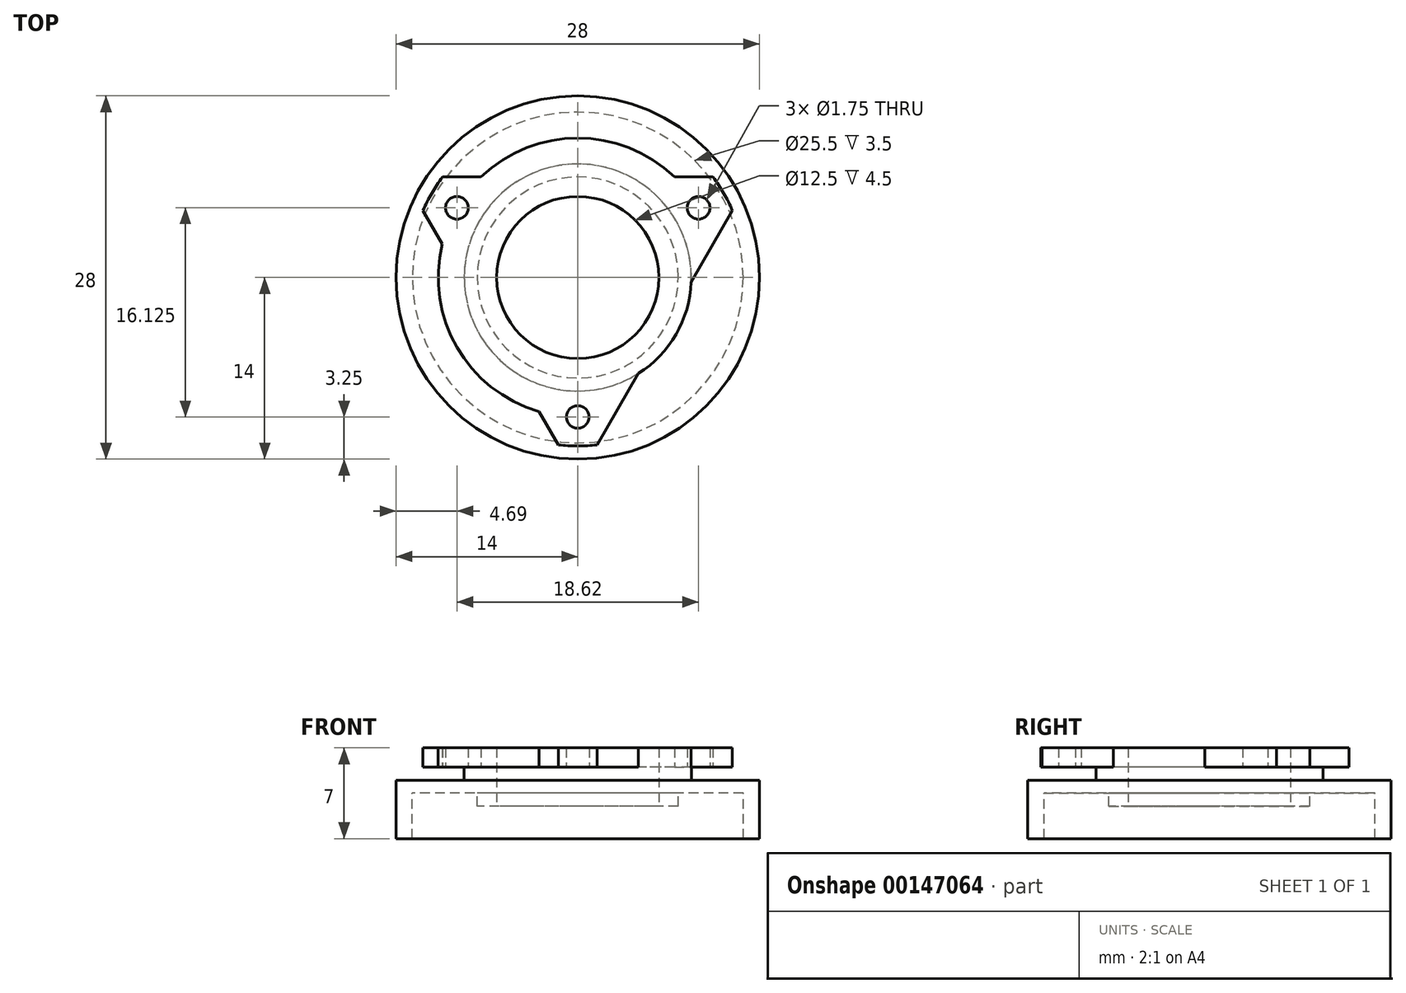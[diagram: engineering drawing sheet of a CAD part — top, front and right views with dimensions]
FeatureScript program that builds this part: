
annotation { "Feature Type Name" : "Feature", "Feature Type Description" : "" }
export const myFeature = defineFeature(function(context is Context, id is Id, definition is map)
    precondition{}
    {
        {
            var Q0;
            Q0=qCreatedBy(makeId("Top.planeOp"),FACE);
            var sketch = newSketch(context, id + "F0", { "sketchPlane" : qUnion([Q0])});
            skCircle(sketch, "E0", {"center": v(0, 0) * mm, "radius": 14 * mm});
            skCircle(sketch, "E1", {"center": v(0, 0) * mm, "radius": 12.75 * mm});
            skCircle(sketch, "E2", {"center": v(0, 0) * mm, "radius": 8.75 * mm});
            skCircle(sketch, "E3", {"center": v(0, 0) * mm, "radius": 7.75 * mm});
            skSolve(sketch);
        }
        {
            var Q0;
            Q0=makeQuery(id+"F0.imprint","IMPRINT",FACE,{"disambiguationData":[TD([[makeQuery(id+"F0.imprint","IMPRINT",EDGE,{"derivedFrom":sQuery(id+"F0.wireOp",EDGE,"E2")}),1.0]])]});
            extrude(context, id + "F1", {"entities" : qUnion([Q0]), "depth" : 2 * mm});
        }
        {
            var Q0;
            Q0=makeQuery(id+"F0.imprint","IMPRINT",FACE,{"disambiguationData":[TD([[makeQuery(id+"F0.imprint","IMPRINT",EDGE,{"derivedFrom":sQuery(id+"F0.wireOp",EDGE,"E1")}),1.0]])]});
            extrude(context, id + "F2", {"entities" : qUnion([Q0]), "operationType" : NewBodyOperationType.ADD, "depth" : 1 * mm});
        }
        {
            var Q0;
            Q0=makeQuery(id+"F0.imprint","IMPRINT",FACE,{"disambiguationData":[TD([[makeQuery(id+"F0.imprint","IMPRINT",EDGE,{"derivedFrom":sQuery(id+"F0.wireOp",EDGE,"E0")}),1.0]])]});
            extrude(context, id + "F3", {"entities" : qUnion([Q0]), "operationType" : NewBodyOperationType.ADD, "oppositeDirection" : true, "depth" : 3.5 * mm, "hasSecondDirection" : true, "secondDirectionOppositeDirection" : false, "secondDirectionDepth" : 1 * mm});
        }
        {
            var Q0;
            Q0=makeQuery(id+"F1.opExtrude","CAP_FACE",FACE,{"disambiguationData":[OSD([sQuery(id+"F0.wireOp",EDGE,"E2"),sQuery(id+"F0.wireOp",EDGE,"E3")])],"isStart":false});
            var sketch = newSketch(context, id + "F4", { "sketchPlane" : qUnion([Q0])});
            skCircle(sketch, "E4", {"center": v(0, 0) * mm, "radius": 10.75 * mm});
            skLineSegment(sketch, "E5", {"start": v(-9.3, 5.38) * mm, "end": v(9.3, 5.38) * mm});
            skLineSegment(sketch, "E6", {"start": v(9.3, 5.38) * mm, "end": v(0, -10.75) * mm});
            skLineSegment(sketch, "E7", {"start": v(0, -10.75) * mm, "end": v(-9.3, 5.38) * mm});
            skCircle(sketch, "E8", {"center": v(-9.3, 5.38) * mm, "radius": 0.88 * mm});
            skCircle(sketch, "E9", {"center": v(0, -10.75) * mm, "radius": 0.88 * mm});
            skCircle(sketch, "E10", {"center": v(9.3, 5.38) * mm, "radius": 0.88 * mm});
            skCircle(sketch, "E11", {"center": v(0, 0) * mm, "radius": 12.99 * mm});
            skCircle(sketch, "E12.0", {"center": v(0, 0) * mm, "radius": 7.75 * mm});
            skCircle(sketch, "E13.0", {"center": v(0, 0) * mm, "radius": 6.25 * mm});
            skLineSegment(sketch, "E14.0", {"start": v(-13.42, 7.75) * mm, "end": v(13.42, 7.75) * mm});
            skLineSegment(sketch, "E14.1", {"start": v(0, -15.5) * mm, "end": v(-13.42, 7.75) * mm});
            skLineSegment(sketch, "E14.2", {"start": v(13.42, 7.75) * mm, "end": v(0, -15.5) * mm});
            skSolve(sketch);
        }
        {
            var Q0;
            {var subQ0=sQuery(id+"F4.wireOp",EDGE,"E14.0");var subQ6=sQuery(id+"F4.wireOp",EDGE,"E4");var subQ10=makeQuery(id+"F4.imprint","INTERSECT",VERTEX,{"disambiguationData":[OD(1.0)],"derivedFrom":[subQ6,subQ0]});Q0=makeQuery(id+"F4.imprint","IMPRINT",FACE,{"disambiguationData":[TD([[makeQuery(id+"F4.imprint","IMPRINT",EDGE,{"disambiguationData":[TD([[subQ10,-1.0]])],"derivedFrom":subQ6}),-1.0]])]});}
            var Q1;
            {var subQ0=sQuery(id+"F4.wireOp",EDGE,"E14.1");var subQ6=sQuery(id+"F4.wireOp",EDGE,"E4");var subQ10=makeQuery(id+"F4.imprint","INTERSECT",VERTEX,{"disambiguationData":[OD(1.0)],"derivedFrom":[subQ6,subQ0]});Q1=makeQuery(id+"F4.imprint","IMPRINT",FACE,{"disambiguationData":[TD([[makeQuery(id+"F4.imprint","IMPRINT",EDGE,{"disambiguationData":[TD([[subQ10,-1.0]])],"derivedFrom":subQ6}),-1.0]])]});}
            var Q2;
            {var subQ0=sQuery(id+"F4.wireOp",EDGE,"E10");var subQ1=sQuery(id+"F4.wireOp",EDGE,"E4");var subQ2=makeQuery(id+"F4.imprint","INTERSECT",VERTEX,{"disambiguationData":[OD(0.0)],"derivedFrom":[subQ1,subQ0]});Q2=makeQuery(id+"F4.imprint","IMPRINT",FACE,{"disambiguationData":[TD([[makeQuery(id+"F4.imprint","IMPRINT",EDGE,{"disambiguationData":[TD([[subQ2,1.0]])],"derivedFrom":subQ1}),-1.0]])]});}
            var Q3;
            {var subQ0=sQuery(id+"F4.wireOp",EDGE,"E14.0");var subQ1=sQuery(id+"F4.wireOp",EDGE,"E4");var subQ2=makeQuery(id+"F4.imprint","INTERSECT",VERTEX,{"disambiguationData":[OD(0.0)],"derivedFrom":[subQ1,subQ0]});Q3=makeQuery(id+"F4.imprint","IMPRINT",FACE,{"disambiguationData":[TD([[makeQuery(id+"F4.imprint","IMPRINT",EDGE,{"disambiguationData":[TD([[subQ2,-1.0]])],"derivedFrom":subQ1}),1.0]])]});}
            var Q4;
            {var subQ0=sQuery(id+"F4.wireOp",EDGE,"E14.0");var subQ1=sQuery(id+"F4.wireOp",EDGE,"E4");var subQ2=makeQuery(id+"F4.imprint","INTERSECT",VERTEX,{"disambiguationData":[OD(1.0)],"derivedFrom":[subQ1,subQ0]});Q4=makeQuery(id+"F4.imprint","IMPRINT",FACE,{"disambiguationData":[TD([[makeQuery(id+"F4.imprint","IMPRINT",EDGE,{"disambiguationData":[TD([[subQ2,-1.0]])],"derivedFrom":subQ1}),1.0]])]});}
            var Q5;
            {var subQ0=sQuery(id+"F4.wireOp",EDGE,"E8");var subQ1=sQuery(id+"F4.wireOp",EDGE,"E5");var subQ2=makeQuery(id+"F4.imprint","INTERSECT",VERTEX,{"derivedFrom":[subQ1,subQ0]});Q5=makeQuery(id+"F4.imprint","IMPRINT",FACE,{"disambiguationData":[TD([[makeQuery(id+"F4.imprint","IMPRINT",EDGE,{"disambiguationData":[TD([[subQ2,-1.0]])],"derivedFrom":subQ1}),-1.0]])]});}
            var Q6;
            {var subQ1=sQuery(id+"F4.wireOp",EDGE,"E4");var subQ5=sQuery(id+"F4.wireOp",EDGE,"E8");var subQ6=makeQuery(id+"F4.imprint","INTERSECT",VERTEX,{"disambiguationData":[OD(1.0)],"derivedFrom":[subQ1,subQ5]});Q6=makeQuery(id+"F4.imprint","IMPRINT",FACE,{"disambiguationData":[TD([[makeQuery(id+"F4.imprint","IMPRINT",EDGE,{"disambiguationData":[TD([[subQ6,-1.0]])],"derivedFrom":subQ1}),1.0]])]});}
            var Q7;
            {var subQ0=sQuery(id+"F4.wireOp",EDGE,"E14.1");var subQ1=sQuery(id+"F4.wireOp",EDGE,"E4");var subQ2=makeQuery(id+"F4.imprint","INTERSECT",VERTEX,{"disambiguationData":[OD(0.0)],"derivedFrom":[subQ1,subQ0]});Q7=makeQuery(id+"F4.imprint","IMPRINT",FACE,{"disambiguationData":[TD([[makeQuery(id+"F4.imprint","IMPRINT",EDGE,{"disambiguationData":[TD([[subQ2,-1.0]])],"derivedFrom":subQ1}),1.0]])]});}
            var Q8;
            {var subQ0=sQuery(id+"F4.wireOp",EDGE,"E14.1");var subQ1=sQuery(id+"F4.wireOp",EDGE,"E4");var subQ2=makeQuery(id+"F4.imprint","INTERSECT",VERTEX,{"disambiguationData":[OD(1.0)],"derivedFrom":[subQ1,subQ0]});Q8=makeQuery(id+"F4.imprint","IMPRINT",FACE,{"disambiguationData":[TD([[makeQuery(id+"F4.imprint","IMPRINT",EDGE,{"disambiguationData":[TD([[subQ2,-1.0]])],"derivedFrom":subQ1}),1.0]])]});}
            var Q9;
            {var subQ1=sQuery(id+"F4.wireOp",EDGE,"E4");var subQ5=sQuery(id+"F4.wireOp",EDGE,"E9");var subQ9=makeQuery(id+"F4.imprint","INTERSECT",VERTEX,{"disambiguationData":[OD(1.0)],"derivedFrom":[subQ1,subQ5]});Q9=makeQuery(id+"F4.imprint","IMPRINT",FACE,{"disambiguationData":[TD([[makeQuery(id+"F4.imprint","IMPRINT",EDGE,{"disambiguationData":[TD([[subQ9,-1.0]])],"derivedFrom":subQ1}),1.0]])]});}
            var Q10;
            {var subQ0=sQuery(id+"F4.wireOp",EDGE,"E14.2");var subQ1=sQuery(id+"F4.wireOp",EDGE,"E4");var subQ2=makeQuery(id+"F4.imprint","INTERSECT",VERTEX,{"disambiguationData":[OD(0.0)],"derivedFrom":[subQ1,subQ0]});Q10=makeQuery(id+"F4.imprint","IMPRINT",FACE,{"disambiguationData":[TD([[makeQuery(id+"F4.imprint","IMPRINT",EDGE,{"disambiguationData":[TD([[subQ2,1.0]])],"derivedFrom":subQ1}),1.0]])]});}
            var Q11;
            {var subQ1=sQuery(id+"F4.wireOp",EDGE,"E4");var subQ5=sQuery(id+"F4.wireOp",EDGE,"E10");var subQ6=makeQuery(id+"F4.imprint","INTERSECT",VERTEX,{"disambiguationData":[OD(0.0)],"derivedFrom":[subQ1,subQ5]});Q11=makeQuery(id+"F4.imprint","IMPRINT",FACE,{"disambiguationData":[TD([[makeQuery(id+"F4.imprint","IMPRINT",EDGE,{"disambiguationData":[TD([[subQ6,1.0]])],"derivedFrom":subQ1}),1.0]])]});}
            var Q12;
            {var subQ0=sQuery(id+"F4.wireOp",EDGE,"E10");var subQ1=sQuery(id+"F4.wireOp",EDGE,"E5");var subQ2=makeQuery(id+"F4.imprint","INTERSECT",VERTEX,{"derivedFrom":[subQ1,subQ0]});Q12=makeQuery(id+"F4.imprint","IMPRINT",FACE,{"disambiguationData":[TD([[makeQuery(id+"F4.imprint","IMPRINT",EDGE,{"disambiguationData":[TD([[subQ2,1.0]])],"derivedFrom":subQ1}),-1.0]])]});}
            var Q13;
            {var subQ1=sQuery(id+"F4.wireOp",EDGE,"E4");var subQ5=sQuery(id+"F4.wireOp",EDGE,"E10");var subQ6=makeQuery(id+"F4.imprint","INTERSECT",VERTEX,{"disambiguationData":[OD(1.0)],"derivedFrom":[subQ1,subQ5]});Q13=makeQuery(id+"F4.imprint","IMPRINT",FACE,{"disambiguationData":[TD([[makeQuery(id+"F4.imprint","IMPRINT",EDGE,{"disambiguationData":[TD([[subQ6,-1.0]])],"derivedFrom":subQ1}),1.0]])]});}
            var Q14;
            {var subQ0=sQuery(id+"F4.wireOp",EDGE,"E9");var subQ1=sQuery(id+"F4.wireOp",EDGE,"E6");var subQ2=makeQuery(id+"F4.imprint","INTERSECT",VERTEX,{"derivedFrom":[subQ1,subQ0]});Q14=makeQuery(id+"F4.imprint","IMPRINT",FACE,{"disambiguationData":[TD([[makeQuery(id+"F4.imprint","IMPRINT",EDGE,{"disambiguationData":[TD([[subQ2,1.0]])],"derivedFrom":subQ1}),-1.0]])]});}
            var Q15;
            {var subQ0=sQuery(id+"F4.wireOp",EDGE,"E14.0");var subQ1=makeQuery(id+"F4.imprint","INTERSECT",VERTEX,{"derivedFrom":[sQuery(id+"F4.wireOp",EDGE,"E12.0"),subQ0]});Q15=makeQuery(id+"F4.imprint","IMPRINT",FACE,{"disambiguationData":[TD([[makeQuery(id+"F4.imprint","IMPRINT",EDGE,{"disambiguationData":[TD([[subQ1,1.0]])],"derivedFrom":subQ0}),1.0]])]});}
            var Q16;
            {var subQ0=sQuery(id+"F4.wireOp",EDGE,"E12.0");var subQ1=sQuery(id+"F4.wireOp",EDGE,"E5");var subQ2=makeQuery(id+"F4.imprint","INTERSECT",VERTEX,{"disambiguationData":[OD(0.0)],"derivedFrom":[subQ1,subQ0]});Q16=makeQuery(id+"F4.imprint","IMPRINT",FACE,{"disambiguationData":[TD([[makeQuery(id+"F4.imprint","IMPRINT",EDGE,{"disambiguationData":[TD([[subQ2,1.0]])],"derivedFrom":subQ1}),1.0]])]});}
            var Q17;
            {var subQ0=sQuery(id+"F4.wireOp",EDGE,"E12.0");var subQ1=sQuery(id+"F4.wireOp",EDGE,"E5");var subQ2=makeQuery(id+"F4.imprint","INTERSECT",VERTEX,{"disambiguationData":[OD(0.0)],"derivedFrom":[subQ1,subQ0]});Q17=makeQuery(id+"F4.imprint","IMPRINT",FACE,{"disambiguationData":[TD([[makeQuery(id+"F4.imprint","IMPRINT",EDGE,{"disambiguationData":[TD([[subQ2,1.0]])],"derivedFrom":subQ1}),-1.0]])]});}
            var Q18;
            {var subQ0=sQuery(id+"F4.wireOp",EDGE,"E12.0");var subQ1=sQuery(id+"F4.wireOp",EDGE,"E7");var subQ2=makeQuery(id+"F4.imprint","INTERSECT",VERTEX,{"disambiguationData":[OD(1.0)],"derivedFrom":[subQ1,subQ0]});Q18=makeQuery(id+"F4.imprint","IMPRINT",FACE,{"disambiguationData":[TD([[makeQuery(id+"F4.imprint","IMPRINT",EDGE,{"disambiguationData":[TD([[subQ2,-1.0]])],"derivedFrom":subQ1}),1.0]])]});}
            var Q19;
            {var subQ0=sQuery(id+"F4.wireOp",EDGE,"E14.1");var subQ1=makeQuery(id+"F4.imprint","INTERSECT",VERTEX,{"derivedFrom":[sQuery(id+"F4.wireOp",EDGE,"E12.0"),subQ0]});Q19=makeQuery(id+"F4.imprint","IMPRINT",FACE,{"disambiguationData":[TD([[makeQuery(id+"F4.imprint","IMPRINT",EDGE,{"disambiguationData":[TD([[subQ1,1.0]])],"derivedFrom":subQ0}),1.0]])]});}
            var Q20;
            {var subQ0=sQuery(id+"F4.wireOp",EDGE,"E12.0");var subQ1=sQuery(id+"F4.wireOp",EDGE,"E7");var subQ2=makeQuery(id+"F4.imprint","INTERSECT",VERTEX,{"disambiguationData":[OD(0.0)],"derivedFrom":[subQ1,subQ0]});Q20=makeQuery(id+"F4.imprint","IMPRINT",FACE,{"disambiguationData":[TD([[makeQuery(id+"F4.imprint","IMPRINT",EDGE,{"disambiguationData":[TD([[subQ2,1.0]])],"derivedFrom":subQ1}),1.0]])]});}
            var Q21;
            {var subQ0=sQuery(id+"F4.wireOp",EDGE,"E12.0");var subQ1=sQuery(id+"F4.wireOp",EDGE,"E6");var subQ2=makeQuery(id+"F4.imprint","INTERSECT",VERTEX,{"disambiguationData":[OD(1.0)],"derivedFrom":[subQ1,subQ0]});Q21=makeQuery(id+"F4.imprint","IMPRINT",FACE,{"disambiguationData":[TD([[makeQuery(id+"F4.imprint","IMPRINT",EDGE,{"disambiguationData":[TD([[subQ2,-1.0]])],"derivedFrom":subQ1}),-1.0]])]});}
            var Q22;
            {var subQ0=sQuery(id+"F4.wireOp",EDGE,"E12.0");var subQ1=sQuery(id+"F4.wireOp",EDGE,"E6");var subQ2=makeQuery(id+"F4.imprint","INTERSECT",VERTEX,{"disambiguationData":[OD(1.0)],"derivedFrom":[subQ1,subQ0]});Q22=makeQuery(id+"F4.imprint","IMPRINT",FACE,{"disambiguationData":[TD([[makeQuery(id+"F4.imprint","IMPRINT",EDGE,{"disambiguationData":[TD([[subQ2,-1.0]])],"derivedFrom":subQ1}),1.0]])]});}
            var Q23;
            {var subQ0=sQuery(id+"F4.wireOp",EDGE,"E14.2");var subQ1=makeQuery(id+"F4.imprint","INTERSECT",VERTEX,{"derivedFrom":[sQuery(id+"F4.wireOp",EDGE,"E12.0"),subQ0]});Q23=makeQuery(id+"F4.imprint","IMPRINT",FACE,{"disambiguationData":[TD([[makeQuery(id+"F4.imprint","IMPRINT",EDGE,{"disambiguationData":[TD([[subQ1,1.0]])],"derivedFrom":subQ0}),1.0]])]});}
            var Q24;
            {var subQ0=sQuery(id+"F4.wireOp",EDGE,"E12.0");var subQ1=sQuery(id+"F4.wireOp",EDGE,"E6");var subQ2=makeQuery(id+"F4.imprint","INTERSECT",VERTEX,{"disambiguationData":[OD(0.0)],"derivedFrom":[subQ1,subQ0]});Q24=makeQuery(id+"F4.imprint","IMPRINT",FACE,{"disambiguationData":[TD([[makeQuery(id+"F4.imprint","IMPRINT",EDGE,{"disambiguationData":[TD([[subQ2,1.0]])],"derivedFrom":subQ1}),1.0]])]});}
            var Q25;
            {var subQ0=sQuery(id+"F4.wireOp",EDGE,"E12.0");var subQ1=sQuery(id+"F4.wireOp",EDGE,"E5");var subQ2=makeQuery(id+"F4.imprint","INTERSECT",VERTEX,{"disambiguationData":[OD(1.0)],"derivedFrom":[subQ1,subQ0]});Q25=makeQuery(id+"F4.imprint","IMPRINT",FACE,{"disambiguationData":[TD([[makeQuery(id+"F4.imprint","IMPRINT",EDGE,{"disambiguationData":[TD([[subQ2,-1.0]])],"derivedFrom":subQ1}),-1.0]])]});}
            var Q26;
            {var subQ0=sQuery(id+"F4.wireOp",EDGE,"E12.0");var subQ1=sQuery(id+"F4.wireOp",EDGE,"E5");var subQ2=makeQuery(id+"F4.imprint","INTERSECT",VERTEX,{"disambiguationData":[OD(1.0)],"derivedFrom":[subQ1,subQ0]});Q26=makeQuery(id+"F4.imprint","IMPRINT",FACE,{"disambiguationData":[TD([[makeQuery(id+"F4.imprint","IMPRINT",EDGE,{"disambiguationData":[TD([[subQ2,-1.0]])],"derivedFrom":subQ1}),1.0]])]});}
            var Q27;
            {var subQ0=sQuery(id+"F4.wireOp",EDGE,"E12.0");var subQ1=sQuery(id+"F4.wireOp",EDGE,"E5");var subQ4=makeQuery(id+"F4.imprint","INTERSECT",VERTEX,{"disambiguationData":[OD(0.0)],"derivedFrom":[subQ1,subQ0]});Q27=makeQuery(id+"F4.imprint","IMPRINT",FACE,{"disambiguationData":[TD([[makeQuery(id+"F4.imprint","IMPRINT",EDGE,{"disambiguationData":[TD([[subQ4,-1.0]])],"derivedFrom":subQ1}),1.0]])]});}
            var Q28;
            {var subQ0=sQuery(id+"F4.wireOp",EDGE,"E12.0");var subQ1=sQuery(id+"F4.wireOp",EDGE,"E5");var subQ2=makeQuery(id+"F4.imprint","INTERSECT",VERTEX,{"disambiguationData":[OD(0.0)],"derivedFrom":[subQ1,subQ0]});Q28=makeQuery(id+"F4.imprint","IMPRINT",FACE,{"disambiguationData":[TD([[makeQuery(id+"F4.imprint","IMPRINT",EDGE,{"disambiguationData":[TD([[subQ2,-1.0]])],"derivedFrom":subQ1}),-1.0]])]});}
            var Q29;
            {var subQ0=sQuery(id+"F4.wireOp",EDGE,"E12.0");var subQ1=sQuery(id+"F4.wireOp",EDGE,"E7");var subQ2=makeQuery(id+"F4.imprint","INTERSECT",VERTEX,{"disambiguationData":[OD(0.0)],"derivedFrom":[subQ1,subQ0]});Q29=makeQuery(id+"F4.imprint","IMPRINT",FACE,{"disambiguationData":[TD([[makeQuery(id+"F4.imprint","IMPRINT",EDGE,{"disambiguationData":[TD([[subQ2,-1.0]])],"derivedFrom":subQ1}),1.0]])]});}
            var Q30;
            {var subQ0=sQuery(id+"F4.wireOp",EDGE,"E12.0");var subQ1=sQuery(id+"F4.wireOp",EDGE,"E6");var subQ2=makeQuery(id+"F4.imprint","INTERSECT",VERTEX,{"disambiguationData":[OD(0.0)],"derivedFrom":[subQ1,subQ0]});Q30=makeQuery(id+"F4.imprint","IMPRINT",FACE,{"disambiguationData":[TD([[makeQuery(id+"F4.imprint","IMPRINT",EDGE,{"disambiguationData":[TD([[subQ2,-1.0]])],"derivedFrom":subQ1}),1.0]])]});}
            var Q31;
            {var subQ0=sQuery(id+"F4.wireOp",EDGE,"E13.0");var subQ1=sQuery(id+"F4.wireOp",EDGE,"E5");var subQ2=makeQuery(id+"F4.imprint","INTERSECT",VERTEX,{"disambiguationData":[OD(1.0)],"derivedFrom":[subQ1,subQ0]});Q31=makeQuery(id+"F4.imprint","IMPRINT",FACE,{"disambiguationData":[TD([[makeQuery(id+"F4.imprint","IMPRINT",EDGE,{"disambiguationData":[TD([[subQ2,-1.0]])],"derivedFrom":subQ1}),-1.0]])]});}
            var Q32;
            {var subQ0=sQuery(id+"F4.wireOp",EDGE,"E13.0");var subQ1=sQuery(id+"F4.wireOp",EDGE,"E6");var subQ2=makeQuery(id+"F4.imprint","INTERSECT",VERTEX,{"disambiguationData":[OD(1.0)],"derivedFrom":[subQ1,subQ0]});Q32=makeQuery(id+"F4.imprint","IMPRINT",FACE,{"disambiguationData":[TD([[makeQuery(id+"F4.imprint","IMPRINT",EDGE,{"disambiguationData":[TD([[subQ2,-1.0]])],"derivedFrom":subQ1}),-1.0]])]});}
            extrude(context, id + "F5", {"entities" : qUnion([Q0, Q1, Q2, Q3, Q4, Q5, Q6, Q7, Q8, Q9, Q10, Q11, Q12, Q13, Q14, Q15, Q16, Q17, Q18, Q19, Q20, Q21, Q22, Q23, Q24, Q25, Q26, Q27, Q28, Q29, Q30, Q31, Q32]), "depth" : 1.5 * mm});
        }
        {
            var Q0;
            {var subQ0=sQuery(id+"F4.wireOp",EDGE,"E12.0");var subQ1=sQuery(id+"F4.wireOp",EDGE,"E5");var subQ2=makeQuery(id+"F4.imprint","INTERSECT",VERTEX,{"disambiguationData":[OD(0.0)],"derivedFrom":[subQ1,subQ0]});Q0=makeQuery(id+"F4.imprint","IMPRINT",FACE,{"disambiguationData":[TD([[makeQuery(id+"F4.imprint","IMPRINT",EDGE,{"disambiguationData":[TD([[subQ2,-1.0]])],"derivedFrom":subQ1}),1.0]])]});}
            var Q1;
            {var subQ0=sQuery(id+"F4.wireOp",EDGE,"E12.0");var subQ1=sQuery(id+"F4.wireOp",EDGE,"E5");var subQ2=makeQuery(id+"F4.imprint","INTERSECT",VERTEX,{"disambiguationData":[OD(0.0)],"derivedFrom":[subQ1,subQ0]});Q1=makeQuery(id+"F4.imprint","IMPRINT",FACE,{"disambiguationData":[TD([[makeQuery(id+"F4.imprint","IMPRINT",EDGE,{"disambiguationData":[TD([[subQ2,-1.0]])],"derivedFrom":subQ1}),-1.0]])]});}
            var Q2;
            {var subQ0=sQuery(id+"F4.wireOp",EDGE,"E12.0");var subQ1=sQuery(id+"F4.wireOp",EDGE,"E7");var subQ2=makeQuery(id+"F4.imprint","INTERSECT",VERTEX,{"disambiguationData":[OD(0.0)],"derivedFrom":[subQ1,subQ0]});Q2=makeQuery(id+"F4.imprint","IMPRINT",FACE,{"disambiguationData":[TD([[makeQuery(id+"F4.imprint","IMPRINT",EDGE,{"disambiguationData":[TD([[subQ2,-1.0]])],"derivedFrom":subQ1}),1.0]])]});}
            var Q3;
            {var subQ0=sQuery(id+"F4.wireOp",EDGE,"E13.0");var subQ1=sQuery(id+"F4.wireOp",EDGE,"E6");var subQ2=makeQuery(id+"F4.imprint","INTERSECT",VERTEX,{"disambiguationData":[OD(1.0)],"derivedFrom":[subQ1,subQ0]});Q3=makeQuery(id+"F4.imprint","IMPRINT",FACE,{"disambiguationData":[TD([[makeQuery(id+"F4.imprint","IMPRINT",EDGE,{"disambiguationData":[TD([[subQ2,-1.0]])],"derivedFrom":subQ1}),-1.0]])]});}
            var Q4;
            {var subQ0=sQuery(id+"F4.wireOp",EDGE,"E12.0");var subQ1=sQuery(id+"F4.wireOp",EDGE,"E6");var subQ2=makeQuery(id+"F4.imprint","INTERSECT",VERTEX,{"disambiguationData":[OD(0.0)],"derivedFrom":[subQ1,subQ0]});Q4=makeQuery(id+"F4.imprint","IMPRINT",FACE,{"disambiguationData":[TD([[makeQuery(id+"F4.imprint","IMPRINT",EDGE,{"disambiguationData":[TD([[subQ2,-1.0]])],"derivedFrom":subQ1}),1.0]])]});}
            var Q5;
            {var subQ0=sQuery(id+"F4.wireOp",EDGE,"E13.0");var subQ1=sQuery(id+"F4.wireOp",EDGE,"E5");var subQ2=makeQuery(id+"F4.imprint","INTERSECT",VERTEX,{"disambiguationData":[OD(1.0)],"derivedFrom":[subQ1,subQ0]});Q5=makeQuery(id+"F4.imprint","IMPRINT",FACE,{"disambiguationData":[TD([[makeQuery(id+"F4.imprint","IMPRINT",EDGE,{"disambiguationData":[TD([[subQ2,-1.0]])],"derivedFrom":subQ1}),-1.0]])]});}
            extrude(context, id + "F6", {"entities" : qUnion([Q0, Q1, Q2, Q3, Q4, Q5]), "operationType" : NewBodyOperationType.ADD, "oppositeDirection" : true, "depth" : 3 * mm});
        }
    });
